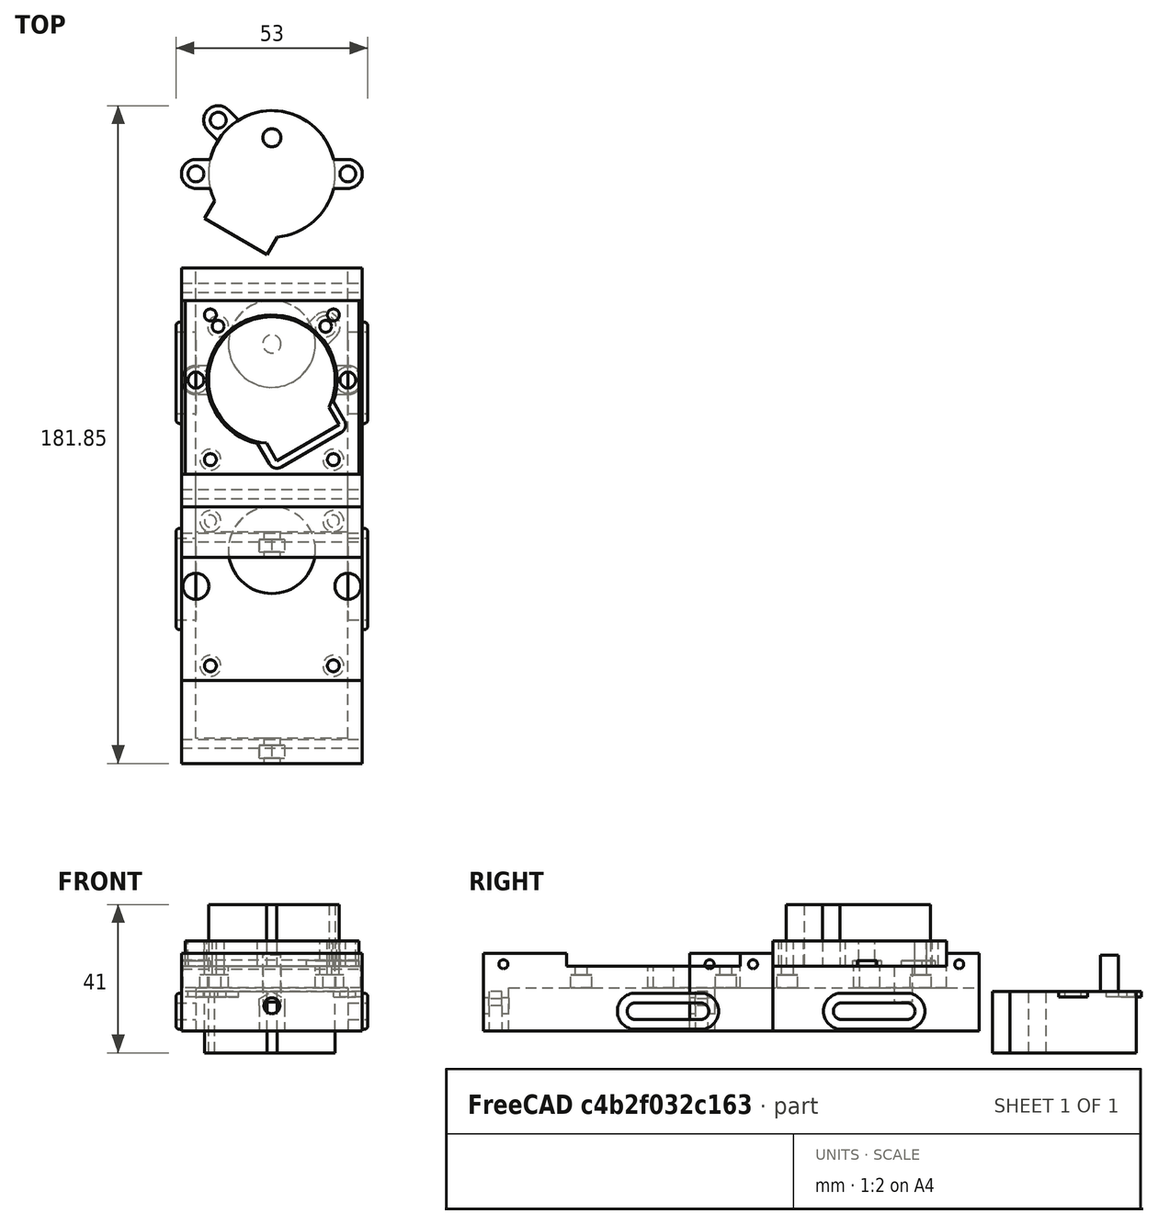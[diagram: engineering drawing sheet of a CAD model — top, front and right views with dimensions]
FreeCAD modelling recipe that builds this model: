
FCSTD DOCUMENT  (FreeCAD 0.19R24291 (Git))
Label: MP35EA
License: All rights reserved
LicenseURL: http://en.wikipedia.org/wiki/All_rights_reserved
objects: Part::Cylinder×70, Part::Box×16, Part::MultiFuse×15, Part::Feature×9, Part::Cut×6, Part::Fillet×4, App::Part×3, Part::Refine×1
note: 121 computed .brp shape members not serialized (recipe doc carries the construction recipe); baked Part::Feature solids carry a one-line shape summary decoded from their .brp

FEATURE [Part::Cylinder] Cylinder  label="Válec"
  Angle = 360
  AttacherType = Attacher::AttachEngine3D
  Height = 17
  Radius = 17.5
FEATURE [Part::Cylinder] Cylinder001  label="Válec001"
  Angle = 360
  AttacherType = Attacher::AttachEngine3D
  Height = 27
  Placement = pos=(0,10,0) rot=(0,0,1;0rad)
  Radius = 2.5
FEATURE [Part::Cylinder] Cylinder002  label="Válec002"
  Angle = 360
  AttacherType = Attacher::AttachEngine3D
  Height = 1.5
  Placement = pos=(21,0,15.5) rot=(0,0,1;0rad)
  Radius = 4
FEATURE [Part::Cylinder] Cylinder003  label="Válec003"
  Angle = 360
  AttacherType = Attacher::AttachEngine3D
  Height = 1.5
  Placement = pos=(-21,0,15.5) rot=(0,0,1;0rad)
  Radius = 4
FEATURE [Part::Box] Box  label="Krychle"
  AttacherType = Attacher::AttachEngine3D
  Height = 1.5
  Length = 42
  Placement = pos=(-21,-4,15.5) rot=(0,0,1;0rad)
  Width = 8
FEATURE [Part::Cylinder] Cylinder004  label="Válec004"
  Angle = 360
  AttacherType = Attacher::AttachEngine3D
  Height = 17
  Radius = 0.1
FEATURE [Part::Feature] Box001001  label="Krychle002"
  Placement = pos=(0,0,0) rot=(0,0,-1;0.523599rad)
  shape: bbox 27.32 x 27.32 x 17 mm, 6 faces (baked)
FEATURE [Part::Cylinder] Cylinder005  label="Válec005"
  Angle = 360
  AttacherType = Attacher::AttachEngine3D
  Height = 2
  Placement = pos=(21,0,15) rot=(0,0,1;0rad)
  Radius = 2.2
FEATURE [Part::Cylinder] Cylinder006  label="Válec006"
  Angle = 360
  AttacherType = Attacher::AttachEngine3D
  Height = 2
  Placement = pos=(-21,0,15) rot=(0,0,1;0rad)
  Radius = 2.2
FEATURE [Part::MultiFuse] Fusion
  Shapes = -> [Cylinder002,Cylinder003,Box001001,Box,Cylinder004,Cylinder,Cylinder001]
FEATURE [Part::MultiFuse] Fusion001
  Shapes = -> [Cylinder005,Cylinder006]
FEATURE [Part::Cut] Cut  label="MP35EA"
  Base = -> Fusion
  Tool = -> Fusion001
FEATURE [Part::Feature] Cut001  label="MP35EA001"
  shape: bbox 50 x 39.82 x 27 mm, 18 faces (baked)
FEATURE [Part::Box] Box001002  label="Krychle003"
  AttacherType = Attacher::AttachEngine3D
  Height = 1.5
  Length = 35
  Placement = pos=(-21,-4,15.5) rot=(0,0,1;0rad)
  Width = 8
FEATURE [Part::Cylinder] Cylinder007  label="Válec007"
  Angle = 360
  AttacherType = Attacher::AttachEngine3D
  Height = 1.5
  Placement = pos=(-21,0,15.5) rot=(0,0,1;0rad)
  Radius = 4
FEATURE [Part::MultiFuse] Fusion002
  Shapes = -> [Cylinder007,Box001002]
FEATURE [Part::Cylinder] Cylinder009  label="Válec009"
  Angle = 360
  AttacherType = Attacher::AttachEngine3D
  Height = 2
  Placement = pos=(-21,0,15) rot=(0,0,1;0rad)
  Radius = 2.2
FEATURE [Part::Cylinder] Cylinder010  label="Válec010"
  Angle = 360
  AttacherType = Attacher::AttachEngine3D
  Height = 2
  Placement = pos=(21,0,15) rot=(0,0,1;0rad)
  Radius = 2.2
FEATURE [Part::MultiFuse] Fusion003
  Shapes = -> [Cylinder010,Cylinder009]
FEATURE [Part::Cut] Cut002
  Base = -> Fusion002
  Placement = pos=(0,0,0) rot=(0,0,1;-0.785398rad)
  Tool = -> Fusion003
FEATURE [Part::MultiFuse] Fusion004
  Shapes = -> [Cut001,Cut002]
FEATURE [Part::Refine] Fusion004001
  Source = -> Fusion004
FEATURE [Part::Feature] Cut003  label="MP35EA002"
  Placement = pos=(0,-57,41) rot=(0,1,0;3.14159rad)
  shape: bbox 50 x 39.82 x 27 mm, 18 faces (baked)
FEATURE [Part::Cylinder] Cylinder112024025003003006010004276196  label="cy100"
  Angle = 360
  AttacherType = Attacher::AttachEngine3D
  Height = 24
  Placement = pos=(17,-39,16) rot=(0,0,1;0rad)
  Radius = 1.65
FEATURE [Part::Cylinder] Cylinder112024025003003006010004276192  label="cy096"
  Angle = 360
  AttacherType = Attacher::AttachEngine3D
  Height = 3.5
  Placement = pos=(-17,-79,18) rot=(0,0,1;0rad)
  Radius = 2.9
FEATURE [Part::Cylinder] Cylinder112024025003003006010004276193  label="cy097"
  Angle = 360
  AttacherType = Attacher::AttachEngine3D
  Height = 24
  Placement = pos=(-17,-39,16) rot=(0,0,1;0rad)
  Radius = 1.65
FEATURE [Part::Cylinder] Cylinder112024025003003006010004276194  label="cy098"
  Angle = 360
  AttacherType = Attacher::AttachEngine3D
  Height = 3.5
  Placement = pos=(-17,-79,18) rot=(0,0,1;0rad)
  Radius = 2.9
FEATURE [Part::Cylinder] Cylinder112024025003003006010004276191  label="cy095"
  Angle = 360
  AttacherType = Attacher::AttachEngine3D
  Height = 24
  Placement = pos=(-17,-79,16) rot=(0,0,1;0rad)
  Radius = 1.65
FEATURE [Part::Cylinder] Cylinder112024025003003006010004276197  label="cy101"
  Angle = 360
  AttacherType = Attacher::AttachEngine3D
  Height = 24
  Placement = pos=(17,-79,16) rot=(0,0,1;0rad)
  Radius = 1.65
FEATURE [Part::Cylinder] Cylinder112024025003003006010004276199  label="cy103"
  Angle = 360
  AttacherType = Attacher::AttachEngine3D
  Height = 3.5
  Placement = pos=(17,-79,18) rot=(0,0,1;0rad)
  Radius = 2.9
FEATURE [Part::Cylinder] Cylinder112024025003003006010004276200  label="cy104"
  Angle = 360
  AttacherType = Attacher::AttachEngine3D
  Height = 24
  Placement = pos=(-17,-79,16) rot=(0,0,1;0rad)
  Radius = 1.65
FEATURE [Part::Cylinder] Cylinder112024025003003006010004276189  label="cy093"
  Angle = 360
  AttacherType = Attacher::AttachEngine3D
  Height = 24
  Placement = pos=(17,-79,16) rot=(0,0,1;0rad)
  Radius = 1.65
FEATURE [Part::Cylinder] Cylinder112024025003003006010004276195  label="cy099"
  Angle = 360
  AttacherType = Attacher::AttachEngine3D
  Height = 3.5
  Placement = pos=(-17,-39,18) rot=(0,0,1;0rad)
  Radius = 2.9
FEATURE [Part::Cylinder] Cylinder112024025003003006010004276198  label="cy102"
  Angle = 360
  AttacherType = Attacher::AttachEngine3D
  Height = 3.5
  Placement = pos=(17,-39,18) rot=(0,0,1;0rad)
  Radius = 2.9
FEATURE [Part::Box] Box021309  label="Krychle292"
  AttacherType = Attacher::AttachEngine3D
  Height = 7
  Length = 48
  Placement = pos=(-24,-83,24) rot=(0,0,1;0rad)
  Width = 48
FEATURE [Part::Cylinder] Cylinder112024025003003006010004276190  label="cy094"
  Angle = 360
  AttacherType = Attacher::AttachEngine3D
  Height = 3.5
  Placement = pos=(17,-79,18) rot=(0,0,1;0rad)
  Radius = 2.9
FEATURE [Part::Box] Box021302  label="Krychle285"
  AttacherType = Attacher::AttachEngine3D
  Height = 21.5
  Length = 50
  Placement = pos=(-25,-106,6) rot=(0,0,1;0rad)
  Width = 80
FEATURE [Part::Cylinder] Cylinder112024025003003006010004276171  label="cy081"
  Angle = 360
  AttacherType = Attacher::AttachEngine3D
  Height = 24
  Placement = pos=(0,-57,24) rot=(0,0,1;0rad)
  Radius = 18
FEATURE [Part::Cylinder] Cylinder112024025003003006010004276172  label="Válec484"
  Angle = 360
  AttacherType = Attacher::AttachEngine3D
  Height = 53
  Placement = pos=(-26.5,-46,11.5) rot=(0,1,0;1.5708rad)
  Radius = 5
FEATURE [Part::Cylinder] Cylinder112024025003003006010004276173  label="cy082"
  Angle = 360
  AttacherType = Attacher::AttachEngine3D
  Height = 24
  Placement = pos=(21,-57,20) rot=(0,0,1;0rad)
  Radius = 1.8
FEATURE [Part::Cylinder] Cylinder112024025003003006010004276175  label="Válec485"
  Angle = 360
  AttacherType = Attacher::AttachEngine3D
  Height = 53
  Placement = pos=(-26.5,-31.5,24.5) rot=(0,1,0;1.5708rad)
  Radius = 1.25
FEATURE [Part::Cylinder] Cylinder112024025003003006010004276174  label="cy083"
  Angle = 360
  AttacherType = Attacher::AttachEngine3D
  Height = 6
  Placement = pos=(21,-57,18) rot=(0,0,1;0rad)
  Radius = 3.6
FEATURE [Part::Box] Box021304  label="Krychle287"
  AttacherType = Attacher::AttachEngine3D
  Height = 12.5
  Length = 42
  Placement = pos=(-21,-99,5.5) rot=(0,0,1;0rad)
  Width = 80
FEATURE [Part::Cylinder] Cylinder112024025003003006010004276178  label="Válec488"
  Angle = 360
  AttacherType = Attacher::AttachEngine3D
  Height = 53
  Placement = pos=(-26.5,-64,11.5) rot=(0,1,0;1.5708rad)
  Radius = 5
FEATURE [Part::Box] Box021305  label="Krychle288"
  AttacherType = Attacher::AttachEngine3D
  Height = 10
  Length = 53
  Placement = pos=(-26.5,-64,6.5) rot=(0,0,1;0rad)
  Width = 18
FEATURE [Part::Cylinder] Cylinder112024025003003006010004276176  label="Válec486"
  Angle = 360
  AttacherType = Attacher::AttachEngine3D
  Height = 53
  Placement = pos=(-26.5,-64,11.5) rot=(0,1,0;1.5708rad)
  Radius = 2.3
FEATURE [Part::Cylinder] Cylinder112024025003003006010004276179  label="cy084"
  Angle = 360
  AttacherType = Attacher::AttachEngine3D
  Height = 24
  Placement = pos=(-21,-57,20) rot=(0,0,1;0rad)
  Radius = 1.8
FEATURE [Part::Box] Box021303  label="Krychle286"
  AttacherType = Attacher::AttachEngine3D
  Height = 4.6
  Length = 53
  Placement = pos=(-26.5,-64,9.2) rot=(0,0,1;0rad)
  Width = 18
FEATURE [Part::Cylinder] Cylinder112024025003003006010004276177  label="Válec487"
  Angle = 360
  AttacherType = Attacher::AttachEngine3D
  Height = 53
  Placement = pos=(-26.5,-46,11.5) rot=(0,1,0;1.5708rad)
  Radius = 2.3
FEATURE [Part::Cylinder] Cylinder112024025003003006010004276180  label="cy085"
  Angle = 360
  AttacherType = Attacher::AttachEngine3D
  Height = 6
  Placement = pos=(-21,-57,18) rot=(0,0,1;0rad)
  Radius = 3.6
FEATURE [Part::Box] Box021307  label="Krychle290"
  AttacherType = Attacher::AttachEngine3D
  Height = 16
  Length = 24
  Placement = pos=(-11.5,-61.5,24) rot=(0,0,-1;1.0472rad)
  Width = 24
FEATURE [Part::Fillet] Fillet028003009002002002002002
  Base = -> Box021307
  Edges = 2 edges r=2.5: [Edge5,Edge7]
FEATURE [Part::Cylinder] Cylinder112024025003003006010004276181  label="Válec489"
  Angle = 360
  AttacherType = Attacher::AttachEngine3D
  Height = 53
  Placement = pos=(-26.5,-100.5,24.5) rot=(0,1,0;1.5708rad)
  Radius = 1.25
FEATURE [Part::Cylinder] Cylinder112024025003003006010004276184  label="cy088"
  Angle = 360
  AttacherType = Attacher::AttachEngine3D
  Height = 30
  Placement = pos=(21,-57,1) rot=(0,0,1;0rad)
  Radius = 2.2
FEATURE [Part::Box] Box021308  label="Krychle291"
  AttacherType = Attacher::AttachEngine3D
  Height = 10
  Length = 50
  Placement = pos=(-25,-83,24) rot=(0,0,1;0rad)
  Width = 48
FEATURE [Part::Cylinder] Cylinder112024025003003006010004276187  label="cy091"
  Angle = 360
  AttacherType = Attacher::AttachEngine3D
  Height = 24
  Placement = pos=(17,-39,16) rot=(0,0,1;0rad)
  Radius = 1.65
FEATURE [Part::Cylinder] Cylinder112024025003003006010004276188  label="cy092"
  Angle = 360
  AttacherType = Attacher::AttachEngine3D
  Height = 3.5
  Placement = pos=(17,-39,18) rot=(0,0,1;0rad)
  Radius = 2.9
FEATURE [Part::Cylinder] Cylinder112024025003003006010004276183  label="cy087"
  Angle = 360
  AttacherType = Attacher::AttachEngine3D
  Height = 30
  Placement = pos=(-21,-57,18) rot=(0,0,1;0rad)
  Radius = 2.2
FEATURE [Part::Cylinder] Cylinder112024025003003006010004276186  label="cy090"
  Angle = 360
  AttacherType = Attacher::AttachEngine3D
  Height = 3.5
  Placement = pos=(-17,-39,18) rot=(0,0,1;0rad)
  Radius = 2.9
FEATURE [Part::Cylinder] Cylinder112024025003003006010004276185  label="cy089"
  Angle = 360
  AttacherType = Attacher::AttachEngine3D
  Height = 24
  Placement = pos=(-17,-39,16) rot=(0,0,1;0rad)
  Radius = 1.65
FEATURE [Part::Cylinder] Cylinder112024025003003006010004276182  label="cy086"
  Angle = 360
  AttacherType = Attacher::AttachEngine3D
  Height = 6
  Placement = pos=(0,-47,18) rot=(0,0,1;0rad)
  Radius = 12
FEATURE [Part::MultiFuse] Fusion005043005007002078086001028019  label="Motor M007"
  Shapes = -> [Cylinder112024025003003006010004276178,Cylinder112024025003003006010004276172,Box021305,Box021302]
FEATURE [Part::MultiFuse] Fusion005043005007002078086001028022
  Shapes = -> [Cylinder112024025003003006010004276193,Cylinder112024025003003006010004276195,Cylinder112024025003003006010004276196,Cylinder112024025003003006010004276198,Cylinder112024025003003006010004276197,Cylinder112024025003003006010004276199,Cylinder112024025003003006010004276200,Cylinder112024025003003006010004276194,Cylinder112024025003003006010004276171,Cylinder112024025003003006010004276183,+1 more]
FEATURE [Part::MultiFuse] Fusion005043005007002078086001028024
  Shapes = -> [Cylinder112024025003003006010004276185,Cylinder112024025003003006010004276192,Cylinder112024025003003006010004276186,Cylinder112024025003003006010004276187,Cylinder112024025003003006010004276189,Cylinder112024025003003006010004276188,Cylinder112024025003003006010004276190,Cylinder112024025003003006010004276191]
FEATURE [Part::Feature] Fusion005043005007002078086001028025  label="matice004"
  Placement = pos=(-53.5,-118.5,24) rot=(1,0,0;3.14159rad)
  shape: bbox 7 x 20 x 14 mm, 15 faces (baked)
FEATURE [Part::MultiFuse] Fusion005043005007002078086001028020  label="Motor vyrezy007"
  Shapes = -> [Box021304,Cylinder112024025003003006010004276176,Cylinder112024025003003006010004276177,Box021303,Cylinder112024025003003006010004276179,Cylinder112024025003003006010004276173,Cylinder112024025003003006010004276180,Cylinder112024025003003006010004276174,Cylinder112024025003003006010004276175,Cylinder112024025003003006010004276181,Cylinder112024025003003006010004276182,Box021308,+2 more]
FEATURE [Part::Cut] Cut018020020009027020002003004004026003005007025004002011  label="AF Moto MP35EA"
  Base = -> Fusion005043005007002078086001028019
  Placement = pos=(0,-57,0) rot=(0,0,1;0rad)
  Tool = -> Fusion005043005007002078086001028020
FEATURE [Part::Fillet] Fillet028003009002002002002003  label="MP35EA base"
  Base = -> Cut018020020009027020002003004004026003005007025004002011
  Edges = 8 edges r=1: [Edge4,Edge7,Edge21,Edge25,Edge153,Edge156,Edge159,Edge160]
FEATURE [Part::Feature] Cut018020020009027020002003004004026003005007025004002012  label="MP35EA003"
  Placement = pos=(0,-57,41) rot=(0,1,0;3.14159rad)
  shape: bbox 50 x 39.82 x 27 mm, 18 faces (baked)
FEATURE [Part::MultiFuse] Fusion005043005007002078086001028023
  Shapes = -> [Fusion005043005007002078086001028022,Cut018020020009027020002003004004026003005007025004002012,Fillet028003009002002002002002]
FEATURE [Part::Cut] Cut018020020009027020002003004004026003005007025004002013  label="MotorPlate MP35EA"
  Base = -> Box021309
  Tool = -> Fusion005043005007002078086001028023
FEATURE [App::Part] Part029  label="MP35EA version"
  Group = -> [Fillet028003009002002002002002,Cut018020020009027020002003004004026003005007025004002012,Fusion005043005007002078086001028023,Fusion005043005007002078086001028022,Box021307,Cylinder112024025003003006010004276171,Cylinder112024025003003006010004276195,Cylinder112024025003003006010004276183,Cylinder112024025003003006010004276194,Cylinder112024025003003006010004276198,+39 more]
  Origin = -> Origin029
FEATURE [App::Part] Part  label="MP35EA004"
  Group = -> [Box001001,Cylinder,Cylinder001,Fusion,Fusion001,Box,Cylinder003,Cylinder002,Cylinder006,Cylinder005,Cylinder004,Cut,Cut001,Fusion002,Fusion003,Cut002,Box001002,Cylinder007,Cylinder010,Cylinder009,Fusion004001,Fusion004]
  Origin = -> Origin
  Placement = pos=(0,-57,41) rot=(0,1,0;3.14159rad)
FEATURE [Part::Cylinder] Cylinder112024025003003006010004276201  label="cy105"
  Angle = 360
  AttacherType = Attacher::AttachEngine3D
  Height = 30
  Placement = pos=(21,-57,1) rot=(0,0,1;0rad)
  Radius = 2.2
FEATURE [Part::Cylinder] Cylinder112024025003003006010004276202  label="cy106"
  Angle = 360
  AttacherType = Attacher::AttachEngine3D
  Height = 24
  Placement = pos=(14.86,-42.15,16) rot=(0,0,1;0rad)
  Radius = 1.65
FEATURE [Part::Box] Box021310  label="Krychle293"
  AttacherType = Attacher::AttachEngine3D
  Height = 16
  Length = 24
  Placement = pos=(-11.5,-61.5,24) rot=(0,0,-1;1.0472rad)
  Width = 24
FEATURE [Part::Cylinder] Cylinder112024025003003006010004276203  label="cy107"
  Angle = 360
  AttacherType = Attacher::AttachEngine3D
  Height = 30
  Placement = pos=(-21,-57,18) rot=(0,0,1;0rad)
  Radius = 2.2
FEATURE [Part::Box] Box021311  label="Krychle294"
  AttacherType = Attacher::AttachEngine3D
  Height = 7
  Length = 48
  Placement = pos=(-24,-83,24) rot=(0,0,1;0rad)
  Width = 48
FEATURE [Part::Cylinder] Cylinder112024025003003006010004276204  label="cy108"
  Angle = 360
  AttacherType = Attacher::AttachEngine3D
  Height = 24
  Placement = pos=(0,-57,24) rot=(0,0,1;0rad)
  Radius = 18
FEATURE [Part::Cylinder] Cylinder112024025003003006010004276205  label="cy109"
  Angle = 360
  AttacherType = Attacher::AttachEngine3D
  Height = 3.5
  Placement = pos=(14.86,-42.15,22) rot=(0,0,1;0rad)
  Radius = 2.9
FEATURE [Part::Cylinder] Cylinder112024025003003006010004276206  label="cy110"
  Angle = 360
  AttacherType = Attacher::AttachEngine3D
  Height = 3.5
  Placement = pos=(-17,-39,18) rot=(0,0,1;0rad)
  Radius = 2.9
FEATURE [Part::Cylinder] Cylinder112024025003003006010004276207  label="cy111"
  Angle = 360
  AttacherType = Attacher::AttachEngine3D
  Height = 3.5
  Placement = pos=(-17,-79,18) rot=(0,0,1;0rad)
  Radius = 2.9
FEATURE [Part::Cylinder] Cylinder112024025003003006010004276208  label="cy112"
  Angle = 360
  AttacherType = Attacher::AttachEngine3D
  Height = 24
  Placement = pos=(-17,-79,16) rot=(0,0,1;0rad)
  Radius = 1.65
FEATURE [Part::Cylinder] Cylinder112024025003003006010004276209  label="cy113"
  Angle = 360
  AttacherType = Attacher::AttachEngine3D
  Height = 3.5
  Placement = pos=(17,-79,18) rot=(0,0,1;0rad)
  Radius = 2.9
FEATURE [Part::Cylinder] Cylinder112024025003003006010004276210  label="cy114"
  Angle = 360
  AttacherType = Attacher::AttachEngine3D
  Height = 24
  Placement = pos=(-14.86,-42.15,16) rot=(0,0,1;0rad)
  Radius = 1.65
FEATURE [Part::Cylinder] Cylinder112024025003003006010004276211  label="cy115"
  Angle = 360
  AttacherType = Attacher::AttachEngine3D
  Height = 24
  Placement = pos=(17,-79,16) rot=(0,0,1;0rad)
  Radius = 1.65
FEATURE [Part::Fillet] Fillet028003009002002002002004
  Base = -> Box021310
  Edges = 2 edges r=2.5: [Edge5,Edge7]
FEATURE [Part::Feature] Fusion004001001  label="Mote3B"
  Placement = pos=(0,-57,41) rot=(0,1,0;3.14159rad)
  shape: bbox 50 x 41.17 x 27 mm, 23 faces (baked)
FEATURE [Part::MultiFuse] Fusion005043005007002078086001028026
  Shapes = -> [Cylinder112024025003003006010004276206,Cylinder112024025003003006010004276202,Cylinder112024025003003006010004276205,Cylinder112024025003003006010004276211,Cylinder112024025003003006010004276209,Cylinder112024025003003006010004276208,Cylinder112024025003003006010004276207,Cylinder112024025003003006010004276204,Cylinder112024025003003006010004276203,Cylinder112024025003003006010004276201,+2 more]
FEATURE [Part::MultiFuse] Fusion005043005007002078086001028027
  Shapes = -> [Fusion005043005007002078086001028026,Fillet028003009002002002002004]
FEATURE [Part::Cut] Cut018020020009027020002003004004026003005007025004002014  label="MotorPlate MP35EA001"
  Base = -> Box021311
  Tool = -> Fusion005043005007002078086001028027
FEATURE [Part::Feature] Cut018020020009027020002003004004026003005007025004002014001  label="MotorPlate MP35EA3B"
  shape: bbox 48 x 48 x 7 mm, 36 faces (baked)
FEATURE [Part::Box] Box021312  label="Krychle295"
  AttacherType = Attacher::AttachEngine3D
  Height = 10
  Length = 50
  Placement = pos=(-25,-83,24) rot=(0,0,1;0rad)
  Width = 48
FEATURE [Part::Cylinder] Cylinder112024025003003006010004276212  label="cy116"
  Angle = 360
  AttacherType = Attacher::AttachEngine3D
  Height = 24
  Placement = pos=(14.86,-42.15,16) rot=(0,0,1;0rad)
  Radius = 1.65
FEATURE [Part::Cylinder] Cylinder112024025003003006010004276213  label="cy117"
  Angle = 360
  AttacherType = Attacher::AttachEngine3D
  Height = 3.5
  Placement = pos=(14.86,-42.15,18) rot=(0,0,1;0rad)
  Radius = 2.9
FEATURE [Part::Cylinder] Cylinder112024025003003006010004276214  label="cy118"
  Angle = 360
  AttacherType = Attacher::AttachEngine3D
  Height = 3.5
  Placement = pos=(-17,-79,18) rot=(0,0,1;0rad)
  Radius = 2.9
FEATURE [Part::Cylinder] Cylinder112024025003003006010004276215  label="Válec490"
  Angle = 360
  AttacherType = Attacher::AttachEngine3D
  Height = 53
  Placement = pos=(-26.5,-100.5,24.5) rot=(0,1,0;1.5708rad)
  Radius = 1.25
FEATURE [Part::Cylinder] Cylinder112024025003003006010004276216  label="Válec491"
  Angle = 360
  AttacherType = Attacher::AttachEngine3D
  Height = 53
  Placement = pos=(-26.5,-46,11.5) rot=(0,1,0;1.5708rad)
  Radius = 2.3
FEATURE [Part::Cylinder] Cylinder112024025003003006010004276217  label="cy119"
  Angle = 360
  AttacherType = Attacher::AttachEngine3D
  Height = 6
  Placement = pos=(-21,-57,18) rot=(0,0,1;0rad)
  Radius = 3.6
FEATURE [Part::Cylinder] Cylinder112024025003003006010004276218  label="cy120"
  Angle = 360
  AttacherType = Attacher::AttachEngine3D
  Height = 24
  Placement = pos=(-14.86,-42.15,16) rot=(0,0,1;0rad)
  Radius = 1.65
FEATURE [Part::Cylinder] Cylinder112024025003003006010004276219  label="cy121"
  Angle = 360
  AttacherType = Attacher::AttachEngine3D
  Height = 3.5
  Placement = pos=(-14.86,-42.15,18) rot=(0,0,1;0rad)
  Radius = 2.9
FEATURE [Part::Cylinder] Cylinder112024025003003006010004276220  label="cy122"
  Angle = 360
  AttacherType = Attacher::AttachEngine3D
  Height = 6
  Placement = pos=(0,-47,18) rot=(0,0,1;0rad)
  Radius = 12
FEATURE [Part::Cylinder] Cylinder112024025003003006010004276221  label="cy123"
  Angle = 360
  AttacherType = Attacher::AttachEngine3D
  Height = 24
  Placement = pos=(21,-57,20) rot=(0,0,1;0rad)
  Radius = 1.8
FEATURE [Part::Cylinder] Cylinder112024025003003006010004276222  label="cy124"
  Angle = 360
  AttacherType = Attacher::AttachEngine3D
  Height = 3.5
  Placement = pos=(17,-79,18) rot=(0,0,1;0rad)
  Radius = 2.9
FEATURE [Part::Cylinder] Cylinder112024025003003006010004276223  label="Válec492"
  Angle = 360
  AttacherType = Attacher::AttachEngine3D
  Height = 53
  Placement = pos=(-26.5,-46,11.5) rot=(0,1,0;1.5708rad)
  Radius = 5
FEATURE [Part::Box] Box021313  label="Krychle296"
  AttacherType = Attacher::AttachEngine3D
  Height = 21.5
  Length = 50
  Placement = pos=(-25,-106,6) rot=(0,0,1;0rad)
  Width = 80
FEATURE [Part::Cylinder] Cylinder112024025003003006010004276224  label="cy125"
  Angle = 360
  AttacherType = Attacher::AttachEngine3D
  Height = 24
  Placement = pos=(17,-79,16) rot=(0,0,1;0rad)
  Radius = 1.65
FEATURE [Part::Cylinder] Cylinder112024025003003006010004276225  label="cy126"
  Angle = 360
  AttacherType = Attacher::AttachEngine3D
  Height = 24
  Placement = pos=(-17,-79,16) rot=(0,0,1;0rad)
  Radius = 1.65
FEATURE [Part::MultiFuse] Fusion005043005007002078086001028029
  Shapes = -> [Cylinder112024025003003006010004276218,Cylinder112024025003003006010004276214,Cylinder112024025003003006010004276219,Cylinder112024025003003006010004276212,Cylinder112024025003003006010004276224,Cylinder112024025003003006010004276213,Cylinder112024025003003006010004276222,Cylinder112024025003003006010004276225]
FEATURE [Part::Cylinder] Cylinder112024025003003006010004276226  label="cy127"
  Angle = 360
  AttacherType = Attacher::AttachEngine3D
  Height = 24
  Placement = pos=(-21,-57,20) rot=(0,0,1;0rad)
  Radius = 1.8
FEATURE [Part::Cylinder] Cylinder112024025003003006010004276227  label="Válec493"
  Angle = 360
  AttacherType = Attacher::AttachEngine3D
  Height = 53
  Placement = pos=(-26.5,-64,11.5) rot=(0,1,0;1.5708rad)
  Radius = 5
FEATURE [Part::Cylinder] Cylinder112024025003003006010004276228  label="Válec494"
  Angle = 360
  AttacherType = Attacher::AttachEngine3D
  Height = 53
  Placement = pos=(-26.5,-31.5,24.5) rot=(0,1,0;1.5708rad)
  Radius = 1.25
FEATURE [Part::Cylinder] Cylinder112024025003003006010004276229  label="Válec495"
  Angle = 360
  AttacherType = Attacher::AttachEngine3D
  Height = 53
  Placement = pos=(-26.5,-64,11.5) rot=(0,1,0;1.5708rad)
  Radius = 2.3
FEATURE [Part::Box] Box021314  label="Krychle297"
  AttacherType = Attacher::AttachEngine3D
  Height = 4.6
  Length = 53
  Placement = pos=(-26.5,-64,9.2) rot=(0,0,1;0rad)
  Width = 18
FEATURE [Part::Box] Box021315  label="Krychle298"
  AttacherType = Attacher::AttachEngine3D
  Height = 10
  Length = 53
  Placement = pos=(-26.5,-64,6.5) rot=(0,0,1;0rad)
  Width = 18
FEATURE [Part::MultiFuse] Fusion005043005007002078086001028030  label="Motor M008"
  Shapes = -> [Cylinder112024025003003006010004276227,Cylinder112024025003003006010004276223,Box021315,Box021313]
FEATURE [Part::Cylinder] Cylinder112024025003003006010004276230  label="cy128"
  Angle = 360
  AttacherType = Attacher::AttachEngine3D
  Height = 6
  Placement = pos=(21,-57,18) rot=(0,0,1;0rad)
  Radius = 3.6
FEATURE [Part::Box] Box021316  label="Krychle299"
  AttacherType = Attacher::AttachEngine3D
  Height = 12.5
  Length = 42
  Placement = pos=(-21,-99,5.5) rot=(0,0,1;0rad)
  Width = 80
FEATURE [Part::Feature] Fusion005043005007002078086001028031  label="matice005"
  Placement = pos=(-53.5,-118.5,24) rot=(1,0,0;3.14159rad)
  shape: bbox 7 x 20 x 14 mm, 15 faces (baked)
FEATURE [Part::MultiFuse] Fusion005043005007002078086001028028  label="Motor vyrezy008"
  Shapes = -> [Box021316,Cylinder112024025003003006010004276229,Cylinder112024025003003006010004276216,Box021314,Cylinder112024025003003006010004276226,Cylinder112024025003003006010004276221,Cylinder112024025003003006010004276217,Cylinder112024025003003006010004276230,Cylinder112024025003003006010004276228,Cylinder112024025003003006010004276215,Cylinder112024025003003006010004276220,Box021312,+2 more]
FEATURE [Part::Cut] Cut018020020009027020002003004004026003005007025004002014002  label="AF Moto MP35EA001"
  Base = -> Fusion005043005007002078086001028030
  Tool = -> Fusion005043005007002078086001028028
FEATURE [Part::Fillet] Fillet028003009002002002002005  label="MP35EA3B ba"
  Base = -> Cut018020020009027020002003004004026003005007025004002014002
  Edges = 8 edges r=1: [Edge4,Edge7,Edge21,Edge25,Edge153,Edge156,Edge159,Edge160]
FEATURE [App::Part] Part030  label="MP35EA3B"
  Group = -> [Cylinder112024025003003006010004276207,Cylinder112024025003003006010004276206,Cylinder112024025003003006010004276208,Cylinder112024025003003006010004276211,Cylinder112024025003003006010004276205,Cylinder112024025003003006010004276210,Cylinder112024025003003006010004276209,Fusion005043005007002078086001028026,Fusion005043005007002078086001028027,Cylinder112024025003003006010004276202,+38 more]
  Origin = -> Origin030
FEATURE [Part::Feature] Fillet028003009002002002002005001  label="MP35EA3B base"
  shape: bbox 53 x 80 x 21.5 mm, 93 faces (baked)
